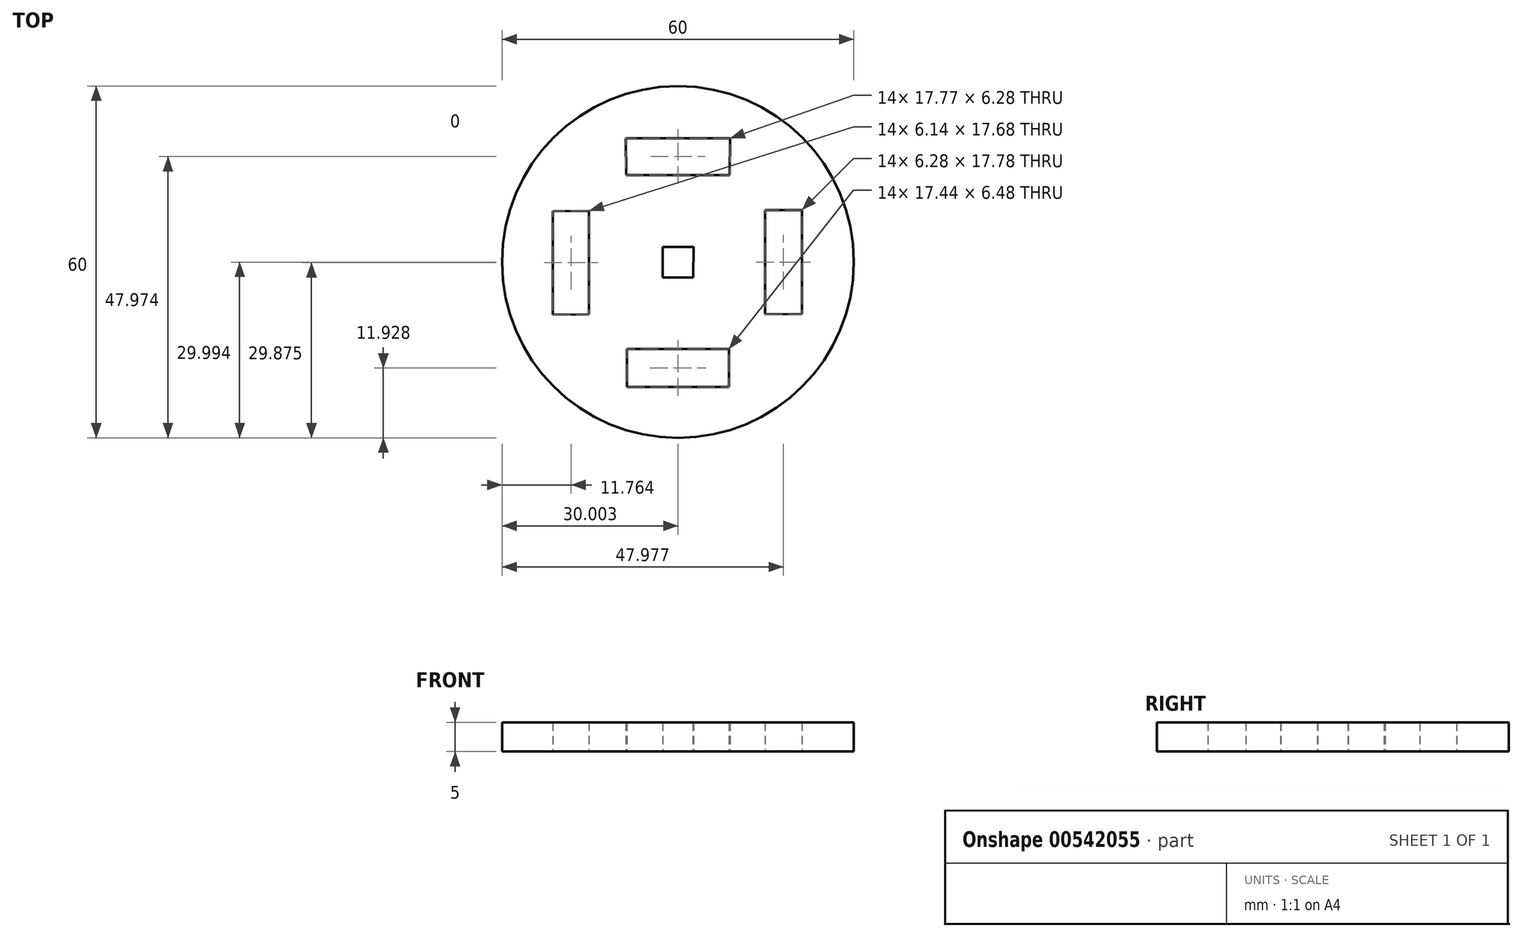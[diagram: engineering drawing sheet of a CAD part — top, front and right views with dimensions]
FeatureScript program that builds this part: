
annotation { "Feature Type Name" : "Feature", "Feature Type Description" : "" }
export const myFeature = defineFeature(function(context is Context, id is Id, definition is map)
    precondition{}
    {
        {
            var Q0;
            Q0=qCreatedBy(makeId("Top.planeOp"),FACE);
            var sketch = newSketch(context, id + "F0", { "sketchPlane" : qUnion([Q0])});
            skCircle(sketch, "E0", {"center": v(358.31, 244.44) * mm, "radius": 30 * mm});
            skLineSegment(sketch, "E1", {"start": v(360.92, 241.83) * mm, "end": v(360.94, 241.81) * mm});
            skLineSegment(sketch, "E2", {"start": v(355.7, 246.99) * mm, "end": v(355.69, 247) * mm});
            skLineSegment(sketch, "E3", {"start": v(388.3, 245.1) * mm, "end": v(388.31, 245.09) * mm});
            skLineSegment(sketch, "E4", {"start": v(379.76, 223.46) * mm, "end": v(379.43, 223.32) * mm});
            skPoint(sketch, "E5.endSnap0", {"position": v(332.59, 254.93) * mm});
            skLineSegment(sketch, "E6", {"start": v(337, 253.13) * mm, "end": v(337, 235.47) * mm});
            skLineSegment(sketch, "E7", {"start": v(343.15, 253.16) * mm, "end": v(343.15, 250.82) * mm});
            skLineSegment(sketch, "E8", {"start": v(349.46, 259.27) * mm, "end": v(367.17, 259.27) * mm});
            skLineSegment(sketch, "E9", {"start": v(373.15, 253.3) * mm, "end": v(373.15, 235.54) * mm});
            skLineSegment(sketch, "E10", {"start": v(367.03, 229.6) * mm, "end": v(349.6, 229.6) * mm});
            skLineSegment(sketch, "E11", {"start": v(349.62, 223.13) * mm, "end": v(367, 223.13) * mm});
            skLineSegment(sketch, "E12", {"start": v(379.43, 253.32) * mm, "end": v(379.43, 235.56) * mm});
            skLineSegment(sketch, "E13", {"start": v(349.43, 265.56) * mm, "end": v(367.2, 265.56) * mm});
            skLineSegment(sketch, "E14", {"start": v(337, 253.13) * mm, "end": v(343.15, 253.16) * mm});
            skLineSegment(sketch, "E15", {"start": v(337, 235.47) * mm, "end": v(343.15, 235.49) * mm});
            skLineSegment(sketch, "E16", {"start": v(349.43, 265.56) * mm, "end": v(349.46, 259.27) * mm});
            skLineSegment(sketch, "E17", {"start": v(367.2, 265.56) * mm, "end": v(367.17, 259.27) * mm});
            skLineSegment(sketch, "E18", {"start": v(355.69, 247) * mm, "end": v(355.69, 241.81) * mm});
            skPoint(sketch, "E19.orphan", {"position": v(317.59, 227.3) * mm});
            skLineSegment(sketch, "E20", {"start": v(355.69, 246.99) * mm, "end": v(360.94, 247) * mm});
            skPoint(sketch, "E20.startSnap0", {"position": v(352.07, 244.2) * mm});
            skPoint(sketch, "E20.endSnap0", {"position": v(364.4, 235.53) * mm});
            skLineSegment(sketch, "E21", {"start": v(355.69, 241.81) * mm, "end": v(360.94, 241.81) * mm});
            skLineSegment(sketch, "E22.trimOffspring", {"start": v(343.15, 250.62) * mm, "end": v(343.15, 235.49) * mm});
            skPoint(sketch, "E23.orphan", {"position": v(317.59, 261.04) * mm});
            skPoint(sketch, "E24.orphan", {"position": v(328.31, 244.44) * mm});
            skPoint(sketch, "E5.end.orphan", {"position": v(332.59, 255.26) * mm});
            skLineSegment(sketch, "E25.trimOffspring", {"start": v(360.95, 247.07) * mm, "end": v(360.92, 241.81) * mm});
            skPoint(sketch, "E26.start.orphan", {"position": v(336.87, 265.42) * mm});
            skPoint(sketch, "E27.orphan", {"position": v(388.31, 244.44) * mm});
            skLineSegment(sketch, "E28.trimOffspring", {"start": v(367.03, 229.6) * mm, "end": v(367, 223.13) * mm});
            skLineSegment(sketch, "E29.trimOffspring", {"start": v(349.6, 229.6) * mm, "end": v(349.62, 223.13) * mm});
            skPoint(sketch, "E30.trimOffspring.end.orphan", {"position": v(375.02, 204.73) * mm});
            skPoint(sketch, "E31.orphan", {"position": v(330.77, 216.9) * mm});
            skPoint(sketch, "E32.trimOffspring.end.orphan", {"position": v(330.77, 271.37) * mm});
            skPoint(sketch, "E33.orphan", {"position": v(375.02, 284.15) * mm});
            skPoint(sketch, "E34.orphan", {"position": v(385.25, 271.37) * mm});
            skLineSegment(sketch, "E35.trimOffspring", {"start": v(373.15, 253.3) * mm, "end": v(379.43, 253.32) * mm});
            skPoint(sketch, "E36.orphan", {"position": v(364.55, 259.27) * mm});
            skPoint(sketch, "E37.orphan", {"position": v(352.07, 259.27) * mm});
            skLineSegment(sketch, "E38.trimOffspring", {"start": v(373.15, 235.54) * mm, "end": v(379.43, 235.56) * mm});
            skLineSegment(sketch, "E39.trimOffspring", {"start": v(379.43, 223.32) * mm, "end": v(379.53, 223.23) * mm});
            skPoint(sketch, "E40.orphan", {"position": v(373.15, 259.27) * mm});
            skPoint(sketch, "E41.orphan", {"position": v(373.15, 250.68) * mm});
            skPoint(sketch, "E42.trimOffspring.start.orphan", {"position": v(355.69, 250.68) * mm});
            skPoint(sketch, "E43.orphan", {"position": v(364.4, 247) * mm});
            skPoint(sketch, "E44.trimOffspring.end.orphan", {"position": v(352.07, 229.13) * mm});
            skLineSegment(sketch, "E45.trimOffspring", {"start": v(360.87, 247) * mm, "end": v(360.95, 247.07) * mm});
            skPoint(sketch, "E46.end.orphan", {"position": v(352.07, 246.98) * mm});
            skPoint(sketch, "E47.trimOffspring.end.orphan", {"position": v(349.37, 235.5) * mm});
            skPoint(sketch, "E48.end.orphan", {"position": v(379.76, 265.42) * mm});
            skLineSegment(sketch, "E49", {"start": v(343.15, 250.82) * mm, "end": v(343.15, 250.62) * mm});
            skPoint(sketch, "E50.end.orphan", {"position": v(336.87, 223.46) * mm});
            skSolve(sketch);
        }
        {
            var Q0;
            {var subQ0=sQuery(id+"F0.wireOp",EDGE,"E4");Q0=makeQuery(id+"F0.imprint","IMPRINT",FACE,{"disambiguationData":[TD([[makeQuery(id+"F0.imprint","IMPRINT",EDGE,{"derivedFrom":subQ0}),1.0]])]});}
            var Q1;
            {var subQ1=sQuery(id+"F0.wireOp",EDGE,"E1");Q1=makeQuery(id+"F0.imprint","IMPRINT",FACE,{"disambiguationData":[TD([[makeQuery(id+"F0.imprint","IMPRINT",EDGE,{"derivedFrom":subQ1}),1.0]])]});}
            extrude(context, id + "F1", {"entities" : qUnion([Q0, Q1]), "depth" : 5 * mm, "offsetDistance" : 25.4 * mm});
        }
    });
